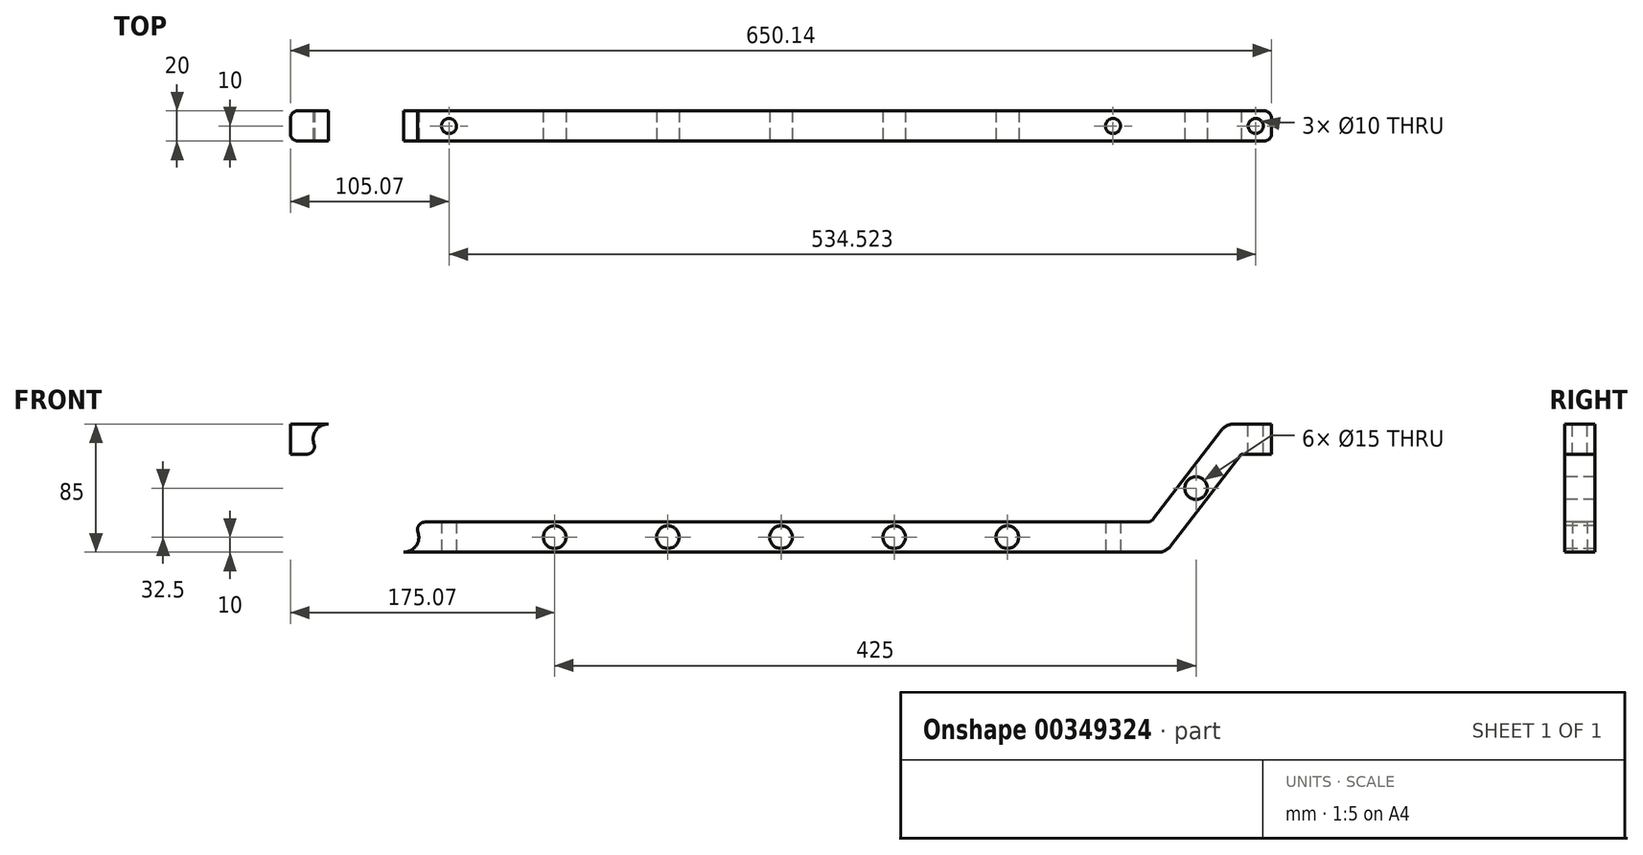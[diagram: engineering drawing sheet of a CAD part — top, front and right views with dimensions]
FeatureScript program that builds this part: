
annotation { "Feature Type Name" : "Feature", "Feature Type Description" : "" }
export const myFeature = defineFeature(function(context is Context, id is Id, definition is map)
    precondition{}
    {
        {
            var Q0;
            Q0=qCreatedBy(makeId("Front.planeOp"),FACE);
            var sketch = newSketch(context, id + "F0", { "sketchPlane" : qUnion([Q0])});
            skArc(sketch, "E0.0.startCap", {"start": v(-307.93, 58.9) * mm, "mid": v(-306.1, 72.93) * mm, "end": v(-292.07, 71.1) * mm});
            skArc(sketch, "E0.0.endCap", {"start": v(-242.07, 6.1) * mm, "mid": v(-243.9, -7.93) * mm, "end": v(-257.93, -6.1) * mm});
            skLineSegment(sketch, "E0.0.left", {"start": v(-292.07, 71.1) * mm, "end": v(-242.07, 6.1) * mm});
            skLineSegment(sketch, "E0.0.right", {"start": v(-307.93, 58.9) * mm, "end": v(-257.93, -6.1) * mm});
            skLineSegment(sketch, "E0.1.left", {"start": v(0, -10) * mm, "end": v(-250, -10) * mm});
            skLineSegment(sketch, "E0.1.right", {"start": v(0, 10) * mm, "end": v(-250, 10) * mm});
            skLineSegment(sketch, "E0.2.left", {"start": v(-300, 55) * mm, "end": v(-320, 55) * mm});
            skLineSegment(sketch, "E0.2.right", {"start": v(-300, 75) * mm, "end": v(-320, 75) * mm});
            skLineSegment(sketch, "E1", {"start": v(0, 0) * mm, "end": v(-75, 0) * mm});
            skLineSegment(sketch, "E2", {"start": v(-75, 0) * mm, "end": v(-150, 0) * mm});
            skCircle(sketch, "E3", {"center": v(-75, 0) * mm, "radius": 7.5 * mm});
            skCircle(sketch, "E4", {"center": v(-150, 0) * mm, "radius": 7.5 * mm});
            skCircle(sketch, "E5", {"center": v(0, 0) * mm, "radius": 7.5 * mm});
            skLineSegment(sketch, "E6", {"start": v(-300, 65) * mm, "end": v(-250, 0) * mm});
            skCircle(sketch, "E7", {"center": v(-275, 32.5) * mm, "radius": 7.5 * mm});
            skLineSegment(sketch, "E8", {"start": v(-300, 75) * mm, "end": v(-325.07, 75) * mm});
            skPoint(sketch, "E8.endSnap0", {"position": v(-310, 75) * mm});
            skLineSegment(sketch, "E9", {"start": v(-325.07, 75) * mm, "end": v(-325.07, 55) * mm});
            skLineSegment(sketch, "E10", {"start": v(-325.07, 55) * mm, "end": v(-319.22, 55) * mm});
            skLineSegment(sketch, "E11.MirrorCS", {"start": v(300, 75) * mm, "end": v(325.07, 75) * mm});
            skLineSegment(sketch, "E12.MirrorCS", {"start": v(325.07, 55) * mm, "end": v(319.22, 55) * mm});
            skCircle(sketch, "E13.MirrorC", {"center": v(75, 0) * mm, "radius": 7.5 * mm});
            skLineSegment(sketch, "E14.MirrorCS", {"start": v(300, 55) * mm, "end": v(320, 55) * mm});
            skLineSegment(sketch, "E15.MirrorCS", {"start": v(300, 75) * mm, "end": v(320, 75) * mm});
            skArc(sketch, "E16.MirrorCS", {"start": v(242.07, 6.1) * mm, "mid": v(243.9, -7.93) * mm, "end": v(257.93, -6.1) * mm});
            skCircle(sketch, "E17.MirrorC", {"center": v(150, 0) * mm, "radius": 7.5 * mm});
            skLineSegment(sketch, "E18.MirrorCS", {"start": v(325.07, 75) * mm, "end": v(325.07, 55) * mm});
            skArc(sketch, "E19.MirrorCS", {"start": v(307.93, 58.9) * mm, "mid": v(306.1, 72.93) * mm, "end": v(292.07, 71.1) * mm});
            skCircle(sketch, "E20.MirrorC", {"center": v(275, 32.5) * mm, "radius": 7.5 * mm});
            skLineSegment(sketch, "E21.MirrorCS", {"start": v(0, 0) * mm, "end": v(75, 0) * mm});
            skPoint(sketch, "E22.MirrorP", {"position": v(310, 75) * mm});
            skLineSegment(sketch, "E23.MirrorCS", {"start": v(0, 10) * mm, "end": v(250, 10) * mm});
            skLineSegment(sketch, "E24.MirrorCS", {"start": v(75, 0) * mm, "end": v(150, 0) * mm});
            skLineSegment(sketch, "E25.MirrorCS", {"start": v(307.93, 58.9) * mm, "end": v(257.93, -6.1) * mm});
            skLineSegment(sketch, "E26.MirrorCS", {"start": v(292.07, 71.1) * mm, "end": v(242.07, 6.1) * mm});
            skLineSegment(sketch, "E27.MirrorCS", {"start": v(300, 65) * mm, "end": v(250, 0) * mm});
            skLineSegment(sketch, "E28.MirrorCS", {"start": v(0, -10) * mm, "end": v(250, -10) * mm});
            skSolve(sketch);
        }
        {
            var Q0;
            {var subQ11=sQuery(id+"F0.wireOp",EDGE,"E0.1.left");Q0=makeQuery(id+"F0.imprint","IMPRINT",FACE,{"disambiguationData":[TD([[makeQuery(id+"F0.imprint","IMPRINT",EDGE,{"derivedFrom":subQ11}),-1.0]])]});}
            var Q1;
            {var subQ0=sQuery(id+"F0.wireOp",EDGE,"E0.0.right");var subQ6=sQuery(id+"F0.wireOp",EDGE,"E0.0.startCap");var subQ9=makeQuery(id+"F0.imprint","INTERSECT",VERTEX,{"derivedFrom":[subQ6,subQ0]});Q1=makeQuery(id+"F0.imprint","IMPRINT",FACE,{"disambiguationData":[TD([[makeQuery(id+"F0.imprint","IMPRINT",EDGE,{"disambiguationData":[TD([[subQ9,-1.0]])],"derivedFrom":subQ6}),-1.0]])]});}
            var Q2;
            {var subQ7=sQuery(id+"F0.wireOp",EDGE,"E9");Q2=makeQuery(id+"F0.imprint","IMPRINT",FACE,{"disambiguationData":[TD([[makeQuery(id+"F0.imprint","IMPRINT",EDGE,{"derivedFrom":subQ7}),1.0]])]});}
            var Q3;
            {var subQ4=sQuery(id+"F0.wireOp",EDGE,"E26.MirrorCS");var subQ5=sQuery(id+"F0.wireOp",EDGE,"E16.MirrorCS");var subQ6=makeQuery(id+"F0.imprint","INTERSECT",VERTEX,{"derivedFrom":[subQ5,subQ4]});Q3=makeQuery(id+"F0.imprint","IMPRINT",FACE,{"disambiguationData":[TD([[makeQuery(id+"F0.imprint","IMPRINT",EDGE,{"disambiguationData":[TD([[subQ6,-1.0]])],"derivedFrom":subQ5}),1.0]])]});}
            var Q4;
            Q4=makeQuery(id+"F0.imprint","IMPRINT",FACE,{"disambiguationData":[TD([[makeQuery(id+"F0.imprint","IMPRINT",EDGE,{"derivedFrom":sQuery(id+"F0.wireOp",EDGE,"E11.MirrorCS")}),-1.0]])]});
            extrude(context, id + "F1", {"entities" : qUnion([Q0, Q1, Q2, Q3, Q4]), "endBound" : BoundingType.SYMMETRIC, "oppositeDirection" : true, "depth" : 20 * mm});
        }
        {
            var Q0;
            Q0=makeQuery(id+"F1.opExtrude","SWEPT_EDGE",EDGE,{"disambiguationData":[OSD([sQuery(id+"F0.wireOp",EDGE,"E0.0.left"),sQuery(id+"F0.wireOp",EDGE,"E0.1.right")])]});
            var Q1;
            Q1=makeQuery(id+"F1.opExtrude","SWEPT_EDGE",EDGE,{"disambiguationData":[OSD([sQuery(id+"F0.wireOp",EDGE,"E23.MirrorCS"),sQuery(id+"F0.wireOp",EDGE,"E26.MirrorCS")])]});
            var Q2;
            Q2=makeQuery(id+"F1.opExtrude","SWEPT_EDGE",EDGE,{"disambiguationData":[OSD([sQuery(id+"F0.wireOp",EDGE,"E0.0.right"),sQuery(id+"F0.wireOp",EDGE,"E0.2.left")])]});
            var Q3;
            Q3=makeQuery(id+"F1.opExtrude","CAP_EDGE",EDGE,{"disambiguationData":[OSD([sQuery(id+"F0.wireOp",EDGE,"E9")])],"isStart":true});
            var Q4;
            Q4=makeQuery(id+"F1.opExtrude","CAP_EDGE",EDGE,{"disambiguationData":[OSD([sQuery(id+"F0.wireOp",EDGE,"E18.MirrorCS")])],"isStart":false});
            var Q5;
            Q5=makeQuery(id+"F1.opExtrude","CAP_EDGE",EDGE,{"disambiguationData":[OSD([sQuery(id+"F0.wireOp",EDGE,"E18.MirrorCS")])],"isStart":true});
            var Q6;
            Q6=makeQuery(id+"F1.opExtrude","CAP_EDGE",EDGE,{"disambiguationData":[OSD([sQuery(id+"F0.wireOp",EDGE,"E9")])],"isStart":false});
            fillet(context, id + "F2", {"entities" : qUnion([Q0, Q1, Q2, Q3, Q4, Q5, Q6]), "radius" : 5 * mm, "tangentPropagation" : true, "allowEdgeOverflow" : false});
        }
        {
            var Q0;
            Q0=makeQuery(id+"F1.opExtrude","SWEPT_FACE",FACE,{"disambiguationData":[OSD([sQuery(id+"F0.wireOp",EDGE,"E8")])]});
            var sketch = newSketch(context, id + "F3", { "sketchPlane" : qUnion([Q0])});
            skLineSegment(sketch, "E29", {"start": v(-325.07, 0) * mm, "end": v(-314.52, 0) * mm});
            skCircle(sketch, "E30", {"center": v(-314.52, 0) * mm, "radius": 5.45 * mm});
            skCircle(sketch, "E31.MirrorC", {"center": v(314.52, 0) * mm, "radius": 5.45 * mm});
            skSolve(sketch);
        }
        {
            var Q0;
            Q0=makeQuery(id+"F1.opExtrude","SWEPT_FACE",FACE,{"disambiguationData":[OSD([sQuery(id+"F0.wireOp",EDGE,"E0.1.left"),sQuery(id+"F0.wireOp",EDGE,"E28.MirrorCS")])]});
            var sketch = newSketch(context, id + "F4", { "sketchPlane" : qUnion([Q0])});
            skLineSegment(sketch, "E32", {"start": v(0, 0) * mm, "end": v(-220, 0) * mm});
            skCircle(sketch, "E33", {"center": v(-220, 0) * mm, "radius": 7.5 * mm});
            skCircle(sketch, "E34.MirrorC", {"center": v(220, 0) * mm, "radius": 7.5 * mm});
            skSolve(sketch);
        }
        {
            var Q0;
            Q0=sQuery(id+"F4.wireOp",VERTEX,"E33.center");
            var Q1;
            Q1=sQuery(id+"F4.wireOp",VERTEX,"E34.MirrorC.center");
            var Q2;
            Q2=sQuery(id+"F3.wireOp",VERTEX,"E31.MirrorC.center");
            var Q3;
            Q3=sQuery(id+"F3.wireOp",VERTEX,"E30.center");
            var Q4;
            Q4=makeQuery(id+"F1.opExtrude","SWEPT_BODY",BODY,{"disambiguationData":[OSD([sQuery(id+"F0.wireOp",EDGE,"E0.0.startCap"),sQuery(id+"F0.wireOp",EDGE,"E0.0.endCap"),sQuery(id+"F0.wireOp",EDGE,"E0.0.left"),sQuery(id+"F0.wireOp",EDGE,"E0.0.right"),sQuery(id+"F0.wireOp",EDGE,"E0.1.left"),sQuery(id+"F0.wireOp",EDGE,"E0.1.right"),sQuery(id+"F0.wireOp",EDGE,"E0.2.left"),sQuery(id+"F0.wireOp",EDGE,"E3"),sQuery(id+"F0.wireOp",EDGE,"E4"),sQuery(id+"F0.wireOp",EDGE,"E7"),sQuery(id+"F0.wireOp",EDGE,"E8"),sQuery(id+"F0.wireOp",EDGE,"E9"),sQuery(id+"F0.wireOp",EDGE,"E10"),sQuery(id+"F0.wireOp",EDGE,"E11.MirrorCS"),sQuery(id+"F0.wireOp",EDGE,"E12.MirrorCS"),sQuery(id+"F0.wireOp",EDGE,"E13.MirrorC"),sQuery(id+"F0.wireOp",EDGE,"E5"),sQuery(id+"F0.wireOp",EDGE,"E14.MirrorCS"),sQuery(id+"F0.wireOp",EDGE,"E15.MirrorCS"),sQuery(id+"F0.wireOp",EDGE,"E16.MirrorCS"),sQuery(id+"F0.wireOp",EDGE,"E17.MirrorC"),sQuery(id+"F0.wireOp",EDGE,"E18.MirrorCS"),sQuery(id+"F0.wireOp",EDGE,"E19.MirrorCS"),sQuery(id+"F0.wireOp",EDGE,"E20.MirrorC"),sQuery(id+"F0.wireOp",EDGE,"E23.MirrorCS"),sQuery(id+"F0.wireOp",EDGE,"E25.MirrorCS"),sQuery(id+"F0.wireOp",EDGE,"E26.MirrorCS"),sQuery(id+"F0.wireOp",EDGE,"E28.MirrorCS")])]});
            hole(context, id + "F5", {"style" : HoleStyle.SIMPLE, "endStyle" : HoleEndStyle.THROUGH, "holeDiameter" : 10 * mm, "isTappedThrough" : true, "tappedDepth" : 12 * mm, "tapClearance" : 3, "locations" : qUnion([Q0, Q1, Q2, Q3]), "scope" : qUnion([Q4])});
        }
    });
